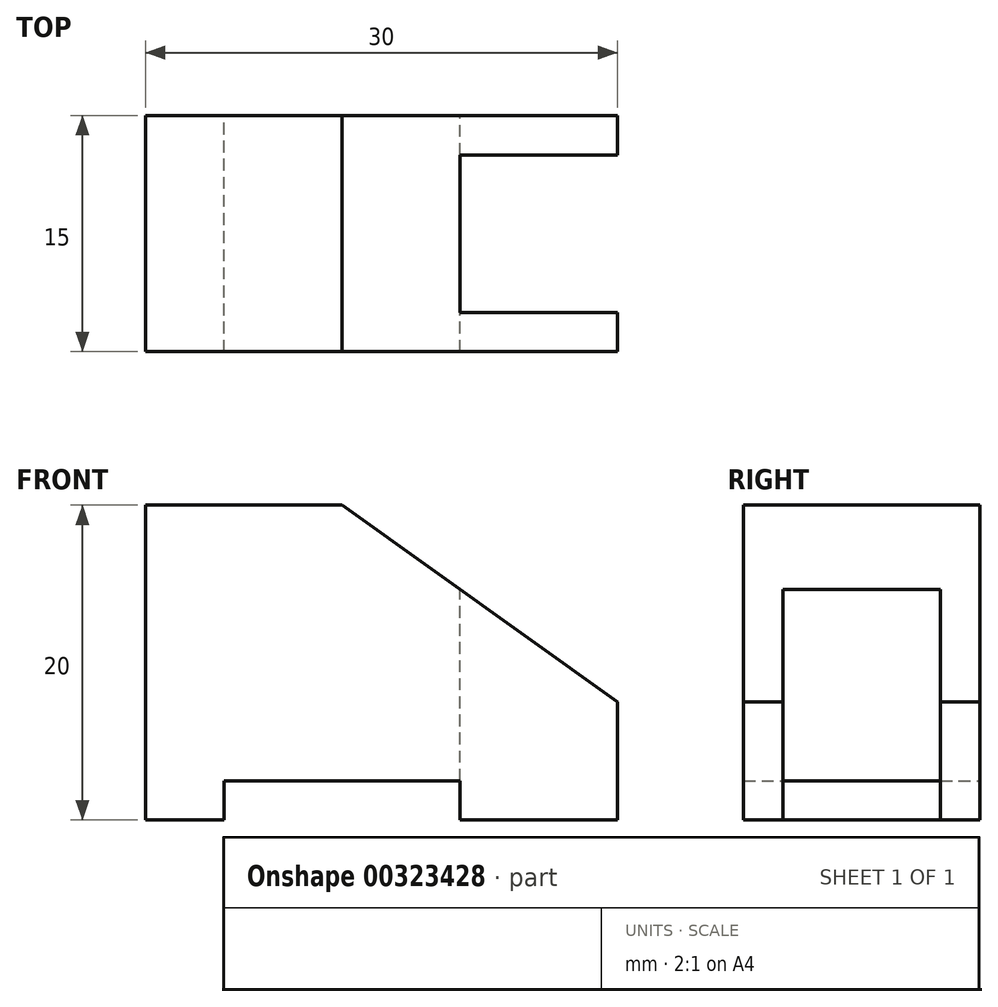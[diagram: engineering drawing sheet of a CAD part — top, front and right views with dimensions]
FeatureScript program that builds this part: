
annotation { "Feature Type Name" : "Feature", "Feature Type Description" : "" }
export const myFeature = defineFeature(function(context is Context, id is Id, definition is map)
    precondition{}
    {
        {
            var Q0;
            Q0=qCreatedBy(makeId("Front.planeOp"),FACE);
            var sketch = newSketch(context, id + "F0", { "sketchPlane" : qUnion([Q0])});
            skLineSegment(sketch, "E0", {"start": v(0, 0) * mm, "end": v(0, 20) * mm});
            skLineSegment(sketch, "E1", {"start": v(0, 20) * mm, "end": v(12.5, 20) * mm});
            skLineSegment(sketch, "E2", {"start": v(12.5, 20) * mm, "end": v(30, 7.5) * mm});
            skLineSegment(sketch, "E3", {"start": v(30, 7.5) * mm, "end": v(30, 0) * mm});
            skLineSegment(sketch, "E4", {"start": v(30, 0) * mm, "end": v(20, 0) * mm});
            skLineSegment(sketch, "E5", {"start": v(20, 0) * mm, "end": v(20, 2.5) * mm});
            skLineSegment(sketch, "E6", {"start": v(20, 2.5) * mm, "end": v(5, 2.5) * mm});
            skLineSegment(sketch, "E7", {"start": v(5, 2.5) * mm, "end": v(5, 0) * mm});
            skLineSegment(sketch, "E8", {"start": v(5, 0) * mm, "end": v(0, 0) * mm});
            skSolve(sketch);
        }
        {
            var Q0;
            Q0=makeQuery(id+"F0.imprint","IMPRINT",FACE,{"disambiguationData":[TD([[makeQuery(id+"F0.imprint","IMPRINT",EDGE,{"derivedFrom":sQuery(id+"F0.wireOp",EDGE,"E0")}),-1.0]])]});
            extrude(context, id + "F1", {"entities" : qUnion([Q0]), "depth" : 15 * mm});
        }
        {
            var Q0;
            Q0=makeQuery(id+"F1.opExtrude","SWEPT_FACE",FACE,{"disambiguationData":[OSD([sQuery(id+"F0.wireOp",EDGE,"E3")])]});
            var sketch = newSketch(context, id + "F2", { "sketchPlane" : qUnion([Q0])});
            skLineSegment(sketch, "E9", {"start": v(-12.5, 0) * mm, "end": v(-2.5, 0) * mm});
            skLineSegment(sketch, "E10", {"start": v(-2.5, 0) * mm, "end": v(-2.5, 15) * mm});
            skLineSegment(sketch, "E11", {"start": v(-2.5, 15) * mm, "end": v(-12.5, 15) * mm});
            skLineSegment(sketch, "E12", {"start": v(-12.5, 15) * mm, "end": v(-12.5, 0) * mm});
            skSolve(sketch);
        }
        {
            var Q0;
            Q0 = qSketchRegion(id + "F2", true);
            extrude(context, id + "F3", {"entities" : qUnion([Q0]), "operationType" : NewBodyOperationType.REMOVE, "oppositeDirection" : true, "depth" : 10 * mm});
        }
    });
